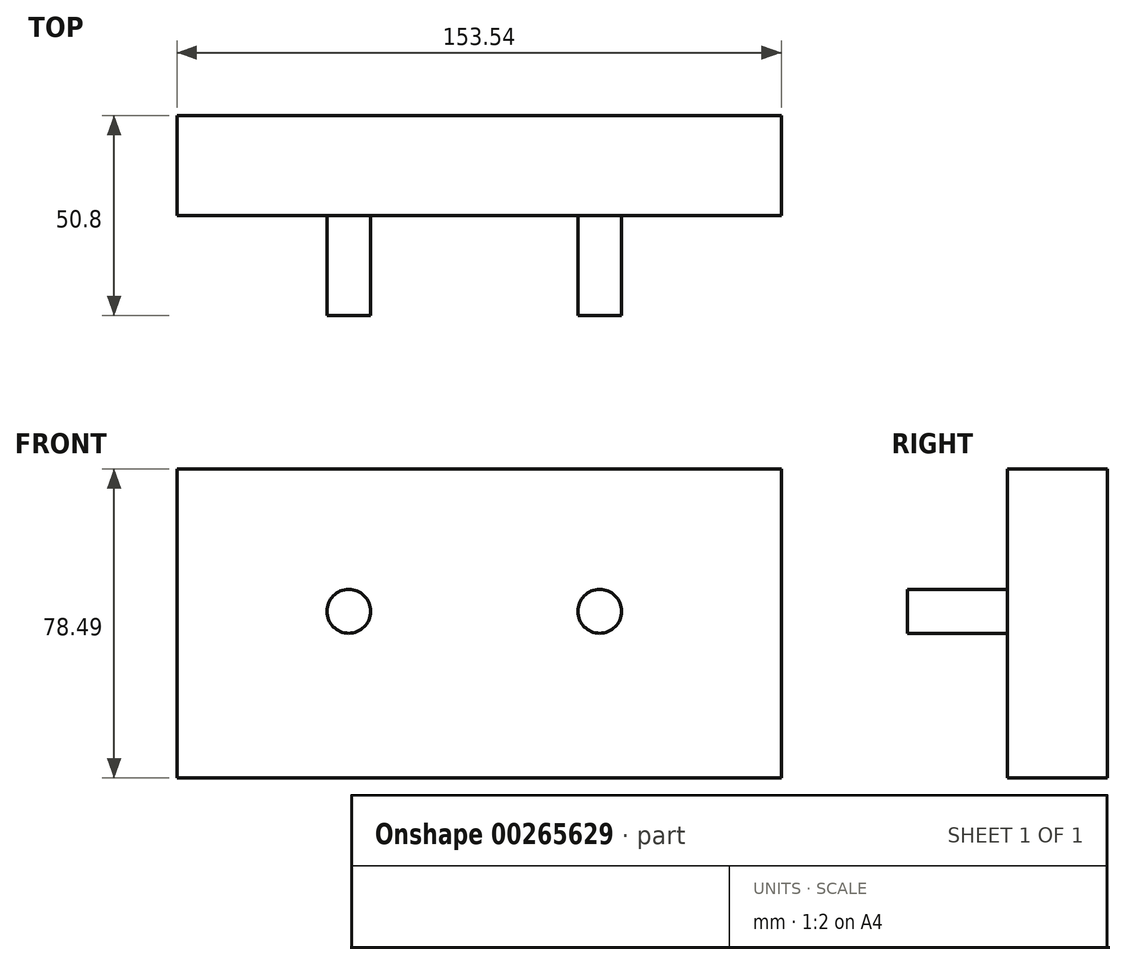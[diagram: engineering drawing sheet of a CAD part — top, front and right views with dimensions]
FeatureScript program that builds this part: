
annotation { "Feature Type Name" : "Feature", "Feature Type Description" : "" }
export const myFeature = defineFeature(function(context is Context, id is Id, definition is map)
    precondition{}
    {
        {
            var Q0;
            Q0=qCreatedBy(makeId("Front.planeOp"),FACE);
            var sketch = newSketch(context, id + "F0", { "sketchPlane" : qUnion([Q0])});
            skLineSegment(sketch, "E0.bottom", {"start": v(0, 0) * mm, "end": v(153.54, 0) * mm});
            skLineSegment(sketch, "E0.top", {"start": v(0, 78.49) * mm, "end": v(153.54, 78.49) * mm});
            skLineSegment(sketch, "E0.left", {"start": v(0, 0) * mm, "end": v(0, 78.49) * mm});
            skLineSegment(sketch, "E0.right", {"start": v(153.54, 0) * mm, "end": v(153.54, 78.49) * mm});
            skSolve(sketch);
        }
        {
            var Q0;
            Q0 = qSketchRegion(id + "F0", true);
            extrude(context, id + "F1", {"entities" : qUnion([Q0]), "depth" : 25.4 * mm});
        }
        {
            var Q0;
            Q0=makeQuery(id+"F1.opExtrude","CAP_FACE",FACE,{"disambiguationData":[OSD([sQuery(id+"F0.wireOp",EDGE,"E0.bottom"),sQuery(id+"F0.wireOp",EDGE,"E0.top"),sQuery(id+"F0.wireOp",EDGE,"E0.left"),sQuery(id+"F0.wireOp",EDGE,"E0.right")])],"isStart":false});
            var sketch = newSketch(context, id + "F2", { "sketchPlane" : qUnion([Q0])});
            skCircle(sketch, "E1", {"center": v(43.64, 42.33) * mm, "radius": 5.56 * mm});
            skLineSegment(sketch, "E2", {"start": v(43.64, 42.33) * mm, "end": v(107.4, 42.33) * mm, "construction": true});
            skCircle(sketch, "E3", {"center": v(107.4, 42.33) * mm, "radius": 5.56 * mm});
            skSolve(sketch);
        }
        {
            var Q0;
            Q0=makeQuery(id+"F2.imprint","IMPRINT",FACE,{"disambiguationData":[TD([[makeQuery(id+"F2.imprint","IMPRINT",EDGE,{"derivedFrom":sQuery(id+"F2.wireOp",EDGE,"E1")}),1.0]])]});
            var Q1;
            Q1=makeQuery(id+"F2.imprint","IMPRINT",FACE,{"disambiguationData":[TD([[makeQuery(id+"F2.imprint","IMPRINT",EDGE,{"derivedFrom":sQuery(id+"F2.wireOp",EDGE,"E3")}),1.0]])]});
            extrude(context, id + "F3", {"entities" : qUnion([Q0, Q1]), "operationType" : NewBodyOperationType.ADD, "depth" : 25.4 * mm});
        }
    });
